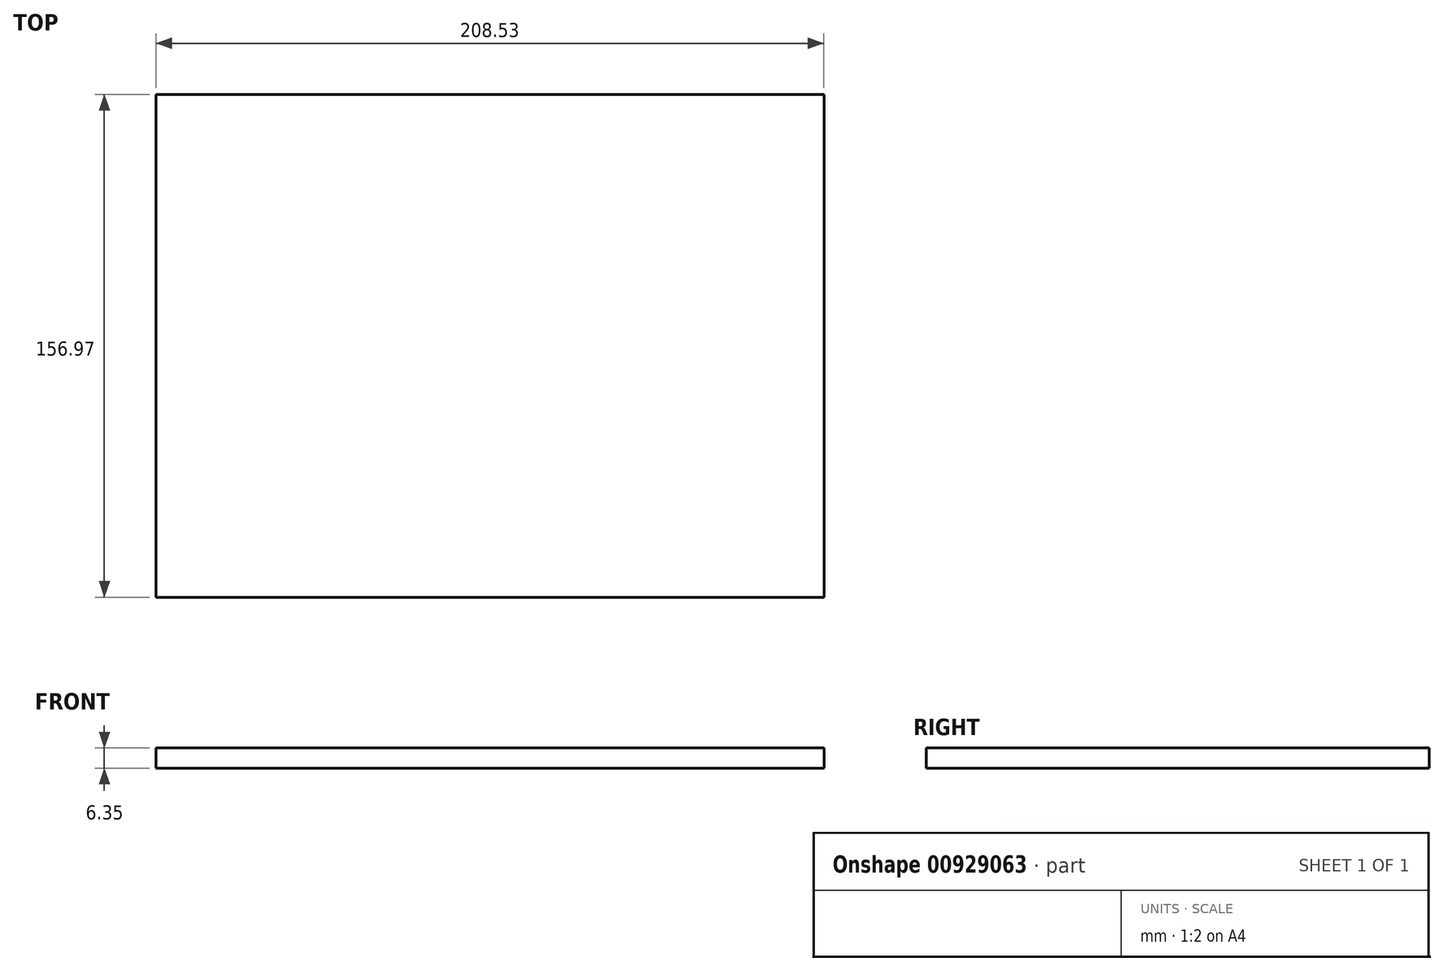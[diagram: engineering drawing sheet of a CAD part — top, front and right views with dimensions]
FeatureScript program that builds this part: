
annotation { "Feature Type Name" : "Feature", "Feature Type Description" : "" }
export const myFeature = defineFeature(function(context is Context, id is Id, definition is map)
    precondition{}
    {
        {
            var Q0;
            Q0=qCreatedBy(makeId("Top.planeOp"),FACE);
            var sketch = newSketch(context, id + "F0", { "sketchPlane" : qUnion([Q0])});
            skLineSegment(sketch, "E0.bottom", {"start": v(0, 0) * mm, "end": v(208.53, 0) * mm});
            skLineSegment(sketch, "E0.top", {"start": v(0, -156.97) * mm, "end": v(208.53, -156.97) * mm});
            skLineSegment(sketch, "E0.left", {"start": v(0, 0) * mm, "end": v(0, -156.97) * mm});
            skLineSegment(sketch, "E0.right", {"start": v(208.53, 0) * mm, "end": v(208.53, -156.97) * mm});
            skSolve(sketch);
        }
        {
            var Q0;
            Q0=makeQuery(id+"F0.imprint","IMPRINT",FACE,{"disambiguationData":[TD([[makeQuery(id+"F0.imprint","IMPRINT",EDGE,{"derivedFrom":sQuery(id+"F0.wireOp",EDGE,"E0.bottom")}),-1.0]])]});
            extrude(context, id + "F1", {"entities" : qUnion([Q0]), "depth" : 6.35 * mm, "offsetDistance" : 25.4 * mm});
        }
    });
